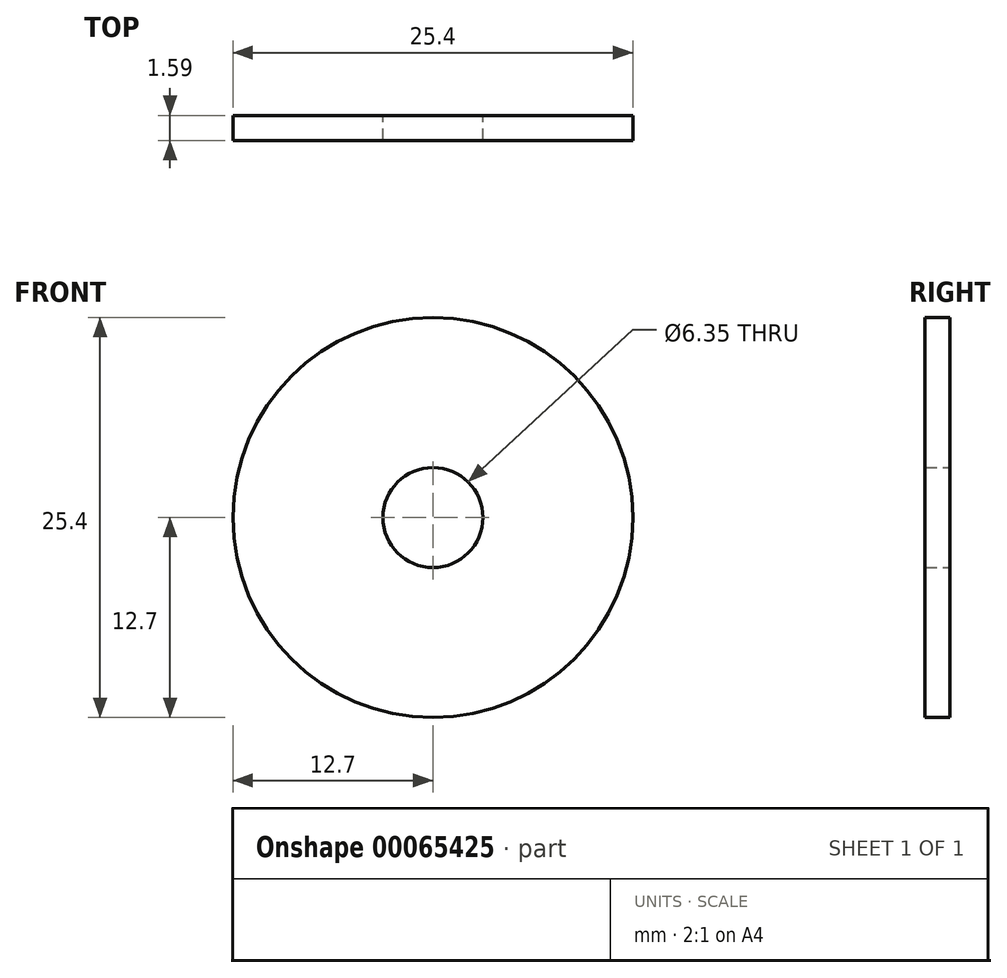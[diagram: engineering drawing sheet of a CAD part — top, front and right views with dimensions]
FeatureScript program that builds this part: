
annotation { "Feature Type Name" : "Feature", "Feature Type Description" : "" }
export const myFeature = defineFeature(function(context is Context, id is Id, definition is map)
    precondition{}
    {
        {
            var Q0;
            Q0=qCreatedBy(makeId("Front.planeOp"),FACE);
            var sketch = newSketch(context, id + "F0", { "sketchPlane" : qUnion([Q0])});
            skCircle(sketch, "E0", {"center": v(0, 0) * mm, "radius": 3.18 * mm});
            skCircle(sketch, "E1", {"center": v(0, 0) * mm, "radius": 12.7 * mm});
            skSolve(sketch);
        }
        {
            var Q0;
            Q0=makeQuery(id+"F0.imprint","IMPRINT",FACE,{"disambiguationData":[TD([[makeQuery(id+"F0.imprint","IMPRINT",EDGE,{"derivedFrom":sQuery(id+"F0.wireOp",EDGE,"E0")}),-1.0]])]});
            extrude(context, id + "F1", {"entities" : qUnion([Q0]), "depth" : 1.59 * mm});
        }
    });
